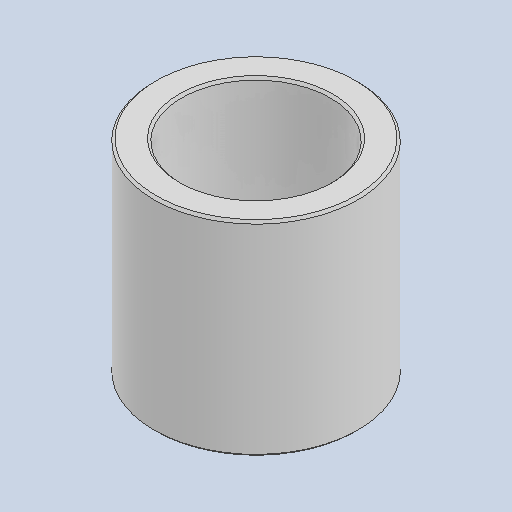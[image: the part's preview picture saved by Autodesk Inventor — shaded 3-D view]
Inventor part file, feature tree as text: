
AUTODESK INVENTOR PART (.ipt)
format: ipt  version: 2024 (Build 280153000, 153)  size: 98,816 bytes
history: native  units: in
note: dims shown in document units (in); Inventor stores cm internally (conversion verified against a paired STEP export)
features: chamfer x1
ambient origin geometry x8: Origin, YZ Plane, XZ Plane, XY Plane, X Axis, Y Axis, Z Axis, Center Point
bodies: Solid1 (feature_tree)
feature tree (1):
  chamfer  "Chamfer1"  [1 undecoded]
note: 1 required parameter value undecoded (feature->parameter linkage not recoverable at this tier; creation-order binding heuristic only, values carry confidence <= 0.55)
